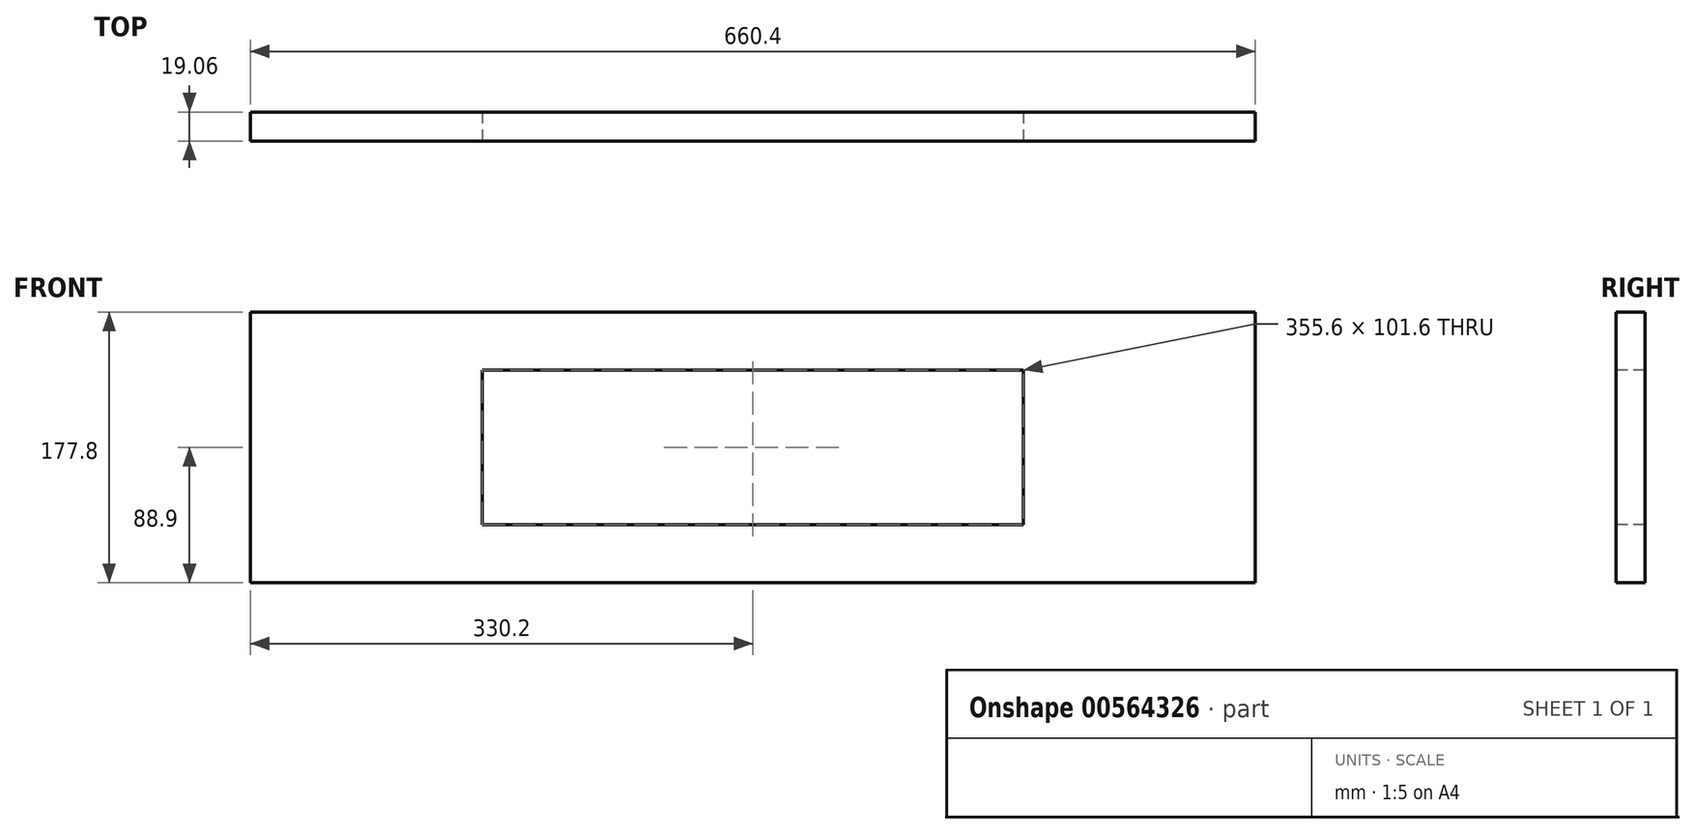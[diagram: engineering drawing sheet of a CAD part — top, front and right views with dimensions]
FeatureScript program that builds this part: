
annotation { "Feature Type Name" : "Feature", "Feature Type Description" : "" }
export const myFeature = defineFeature(function(context is Context, id is Id, definition is map)
    precondition{}
    {
        {
            var Q0;
            Q0=qCreatedBy(makeId("Right.planeOp"),FACE);
            var sketch = newSketch(context, id + "F0", { "sketchPlane" : qUnion([Q0])});
            skLineSegment(sketch, "E0.bottom", {"start": v(-9.53, 88.9) * mm, "end": v(9.52, 88.9) * mm});
            skLineSegment(sketch, "E0.top", {"start": v(-9.52, -88.9) * mm, "end": v(9.53, -88.9) * mm});
            skLineSegment(sketch, "E0.left", {"start": v(-9.53, 88.9) * mm, "end": v(-9.52, -88.9) * mm});
            skLineSegment(sketch, "E0.right", {"start": v(9.52, 88.9) * mm, "end": v(9.53, -88.9) * mm});
            skPoint(sketch, "E0.middle", {"position": v(0, 0) * mm});
            skSolve(sketch);
        }
        {
            var Q0;
            Q0 = qSketchRegion(id + "F0", true);
            extrude(context, id + "F1", {"entities" : qUnion([Q0]), "endBound" : BoundingType.SYMMETRIC, "depth" : 660.4 * mm, "offsetDistance" : 25.4 * mm});
        }
        {
            var Q0;
            Q0=makeQuery(id+"F1.opExtrude","SWEPT_FACE",FACE,{"disambiguationData":[OSD([sQuery(id+"F0.wireOp",EDGE,"E0.left")])]});
            var sketch = newSketch(context, id + "F2", { "sketchPlane" : qUnion([Q0])});
            skLineSegment(sketch, "E1", {"start": v(0, 65.04) * mm, "end": v(0, -73.96) * mm, "construction": true});
            skLineSegment(sketch, "E2.bottom", {"start": v(-177.8, 50.8) * mm, "end": v(177.8, 50.8) * mm});
            skLineSegment(sketch, "E2.top", {"start": v(-177.8, -50.8) * mm, "end": v(177.8, -50.8) * mm});
            skLineSegment(sketch, "E2.left", {"start": v(-177.8, 50.8) * mm, "end": v(-177.8, -50.8) * mm});
            skLineSegment(sketch, "E2.right", {"start": v(177.8, 50.8) * mm, "end": v(177.8, -50.8) * mm});
            skPoint(sketch, "E2.middle", {"position": v(0, 0) * mm});
            skSolve(sketch);
        }
        {
            var Q0;
            Q0 = qSketchRegion(id + "F2", true);
            extrude(context, id + "F3", {"entities" : qUnion([Q0]), "operationType" : NewBodyOperationType.REMOVE, "oppositeDirection" : true, "depth" : 25.4 * mm, "offsetDistance" : 25.4 * mm});
        }
    });
